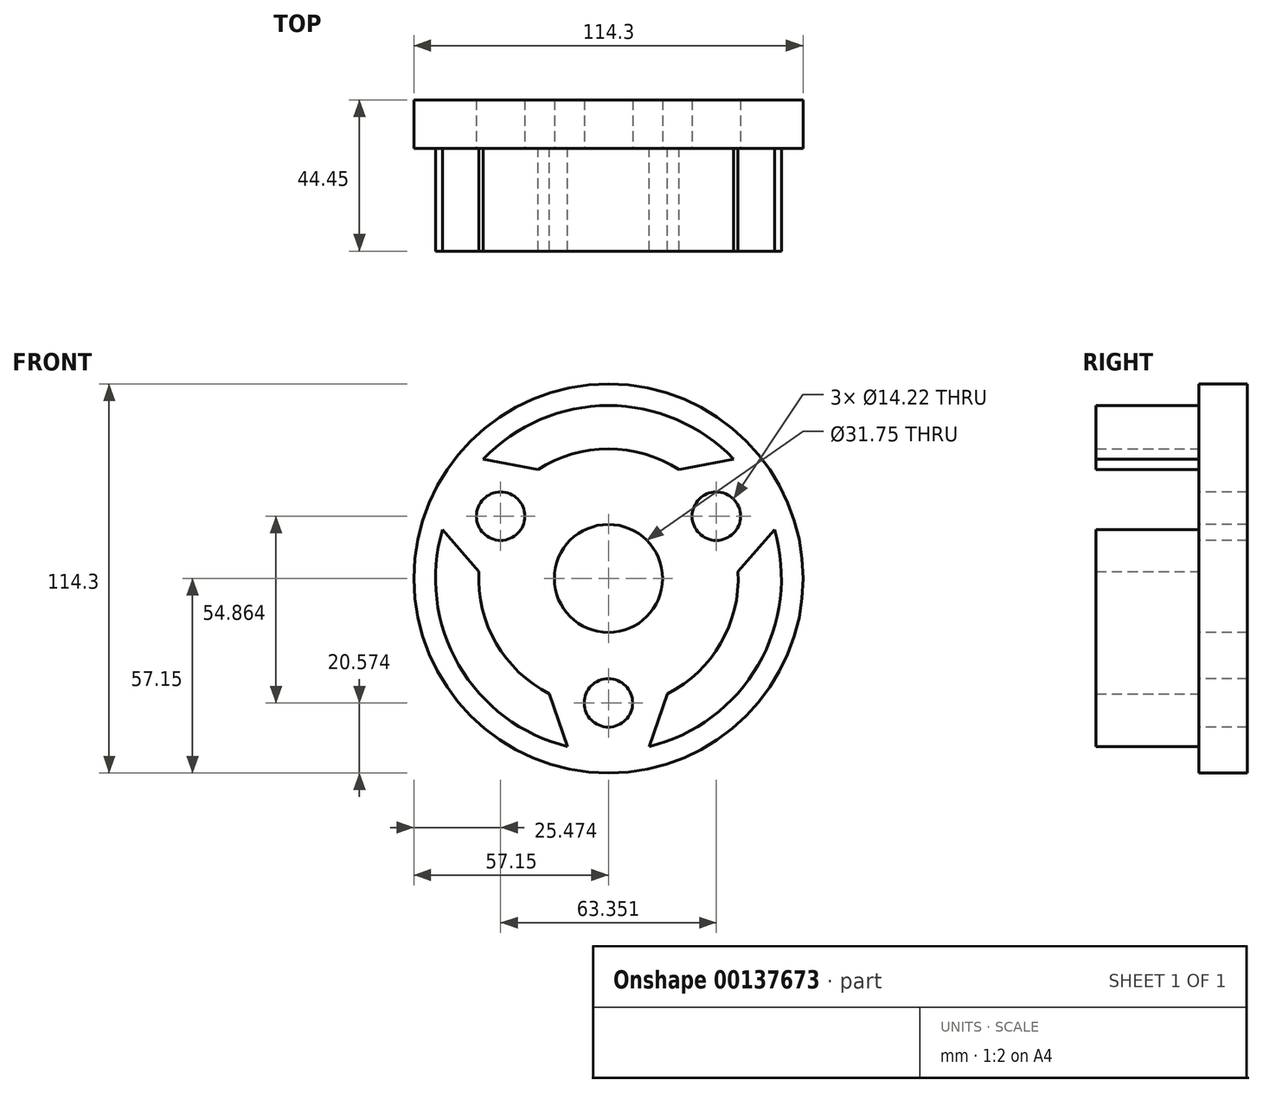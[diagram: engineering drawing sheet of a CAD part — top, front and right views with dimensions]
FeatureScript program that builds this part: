
annotation { "Feature Type Name" : "Feature", "Feature Type Description" : "" }
export const myFeature = defineFeature(function(context is Context, id is Id, definition is map)
    precondition{}
    {
        {
            var Q0;
            Q0=qCreatedBy(makeId("Front.planeOp"),FACE);
            var sketch = newSketch(context, id + "F0", { "sketchPlane" : qUnion([Q0])});
            skCircle(sketch, "E0", {"center": v(0, 0) * mm, "radius": 57.15 * mm});
            skSolve(sketch);
        }
        {
            var Q0;
            Q0 = qSketchRegion(id + "F0", true);
            extrude(context, id + "F1", {"entities" : qUnion([Q0]), "depth" : 14.22 * mm});
        }
        {
            var Q0;
            Q0=makeQuery(id+"F1.opExtrude","CAP_FACE",FACE,{"disambiguationData":[OSD([sQuery(id+"F0.wireOp",EDGE,"E0")])],"isStart":false});
            var sketch = newSketch(context, id + "F2", { "sketchPlane" : qUnion([Q0])});
            skCircle(sketch, "E1", {"center": v(0, -36.58) * mm, "radius": 7.11 * mm});
            skCircle(sketch, "E2.1.0", {"center": v(31.68, 18.29) * mm, "radius": 7.11 * mm});
            skCircle(sketch, "E2.2.0", {"center": v(-31.68, 18.29) * mm, "radius": 7.11 * mm});
            skPoint(sketch, "E2.center", {"position": v(0, 0) * mm});
            skCircle(sketch, "E3", {"center": v(0, 0) * mm, "radius": 15.88 * mm});
            skSolve(sketch);
        }
        {
            var Q0;
            Q0 = qSketchRegion(id + "F2", true);
            extrude(context, id + "F3", {"entities" : qUnion([Q0]), "operationType" : NewBodyOperationType.REMOVE, "endBound" : BoundingType.THROUGH_ALL, "oppositeDirection" : true, "depth" : 25.4 * mm});
        }
        {
            var Q0;
            Q0=makeQuery(id+"F1.opExtrude","CAP_FACE",FACE,{"disambiguationData":[OSD([sQuery(id+"F0.wireOp",EDGE,"E0")])],"isStart":false});
            var sketch = newSketch(context, id + "F4", { "sketchPlane" : qUnion([Q0])});
            skArc(sketch, "E4", {"start": v(-48.74, 14.3) * mm, "mid": v(-44, -25.4) * mm, "end": v(-11.98, -49.37) * mm});
            skArc(sketch, "E5", {"start": v(-38.05, 1.96) * mm, "mid": v(-33, -19.05) * mm, "end": v(-17.33, -33.93) * mm});
            skArc(sketch, "E6.trimOffspring", {"start": v(36.76, 35.06) * mm, "mid": v(0, 50.8) * mm, "end": v(-36.76, 35.06) * mm});
            skArc(sketch, "E7.trimOffspring", {"start": v(20.72, 31.97) * mm, "mid": v(0, 38.1) * mm, "end": v(-20.72, 31.97) * mm});
            skArc(sketch, "E8.trimOffspring", {"start": v(17.33, -33.93) * mm, "mid": v(33, -19.05) * mm, "end": v(38.05, 1.96) * mm});
            skArc(sketch, "E9.trimOffspring", {"start": v(11.98, -49.37) * mm, "mid": v(44, -25.4) * mm, "end": v(48.74, 14.3) * mm});
            skPoint(sketch, "E10.center.orphan", {"position": v(0, -36.58) * mm});
            skLineSegment(sketch, "E11", {"start": v(-17.33, -33.93) * mm, "end": v(-11.98, -49.37) * mm});
            skLineSegment(sketch, "E12", {"start": v(-48.74, 14.3) * mm, "end": v(-38.05, 1.96) * mm});
            skLineSegment(sketch, "E13", {"start": v(-36.76, 35.06) * mm, "end": v(-20.72, 31.97) * mm});
            skLineSegment(sketch, "E14", {"start": v(36.76, 35.06) * mm, "end": v(20.72, 31.97) * mm});
            skLineSegment(sketch, "E15", {"start": v(38.05, 1.96) * mm, "end": v(48.74, 14.3) * mm});
            skLineSegment(sketch, "E16", {"start": v(17.33, -33.93) * mm, "end": v(11.98, -49.37) * mm});
            skSolve(sketch);
        }
        {
            var Q0;
            Q0=makeQuery(id+"F4.imprint","IMPRINT",FACE,{"disambiguationData":[TD([[makeQuery(id+"F4.imprint","IMPRINT",EDGE,{"derivedFrom":sQuery(id+"F4.wireOp",EDGE,"E6.trimOffspring")}),1.0]])]});
            var Q1;
            Q1=makeQuery(id+"F4.imprint","IMPRINT",FACE,{"disambiguationData":[TD([[makeQuery(id+"F4.imprint","IMPRINT",EDGE,{"derivedFrom":sQuery(id+"F4.wireOp",EDGE,"E4")}),1.0]])]});
            var Q2;
            Q2=makeQuery(id+"F4.imprint","IMPRINT",FACE,{"disambiguationData":[TD([[makeQuery(id+"F4.imprint","IMPRINT",EDGE,{"derivedFrom":sQuery(id+"F4.wireOp",EDGE,"E8.trimOffspring")}),-1.0]])]});
            extrude(context, id + "F5", {"entities" : qUnion([Q0, Q1, Q2]), "operationType" : NewBodyOperationType.ADD, "depth" : 30.23 * mm});
        }
    });
